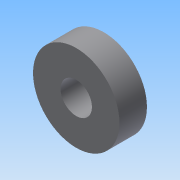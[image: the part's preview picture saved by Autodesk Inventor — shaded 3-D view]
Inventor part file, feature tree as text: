
AUTODESK INVENTOR PART (.ipt)
format: ipt  version: 2015 (Build 190159000, 159)  size: 78,336 bytes
history: native  units: in
note: dims shown in document units (in); Inventor stores cm internally (conversion verified against a paired STEP export)
features: extrude x1, sketch x1
ambient origin geometry x8: Origin, YZ Plane, XZ Plane, XY Plane, X Axis, Y Axis, Z Axis, Center Point
bodies: Solid1 (feature_tree)
feature tree (2):
  extrude  "Extrusion1"  Depth=0.2756in
  sketch  "Sketch1"  dims[d0=0.315in d1=0.8661in d2=0.2756in d3=0.0in]
